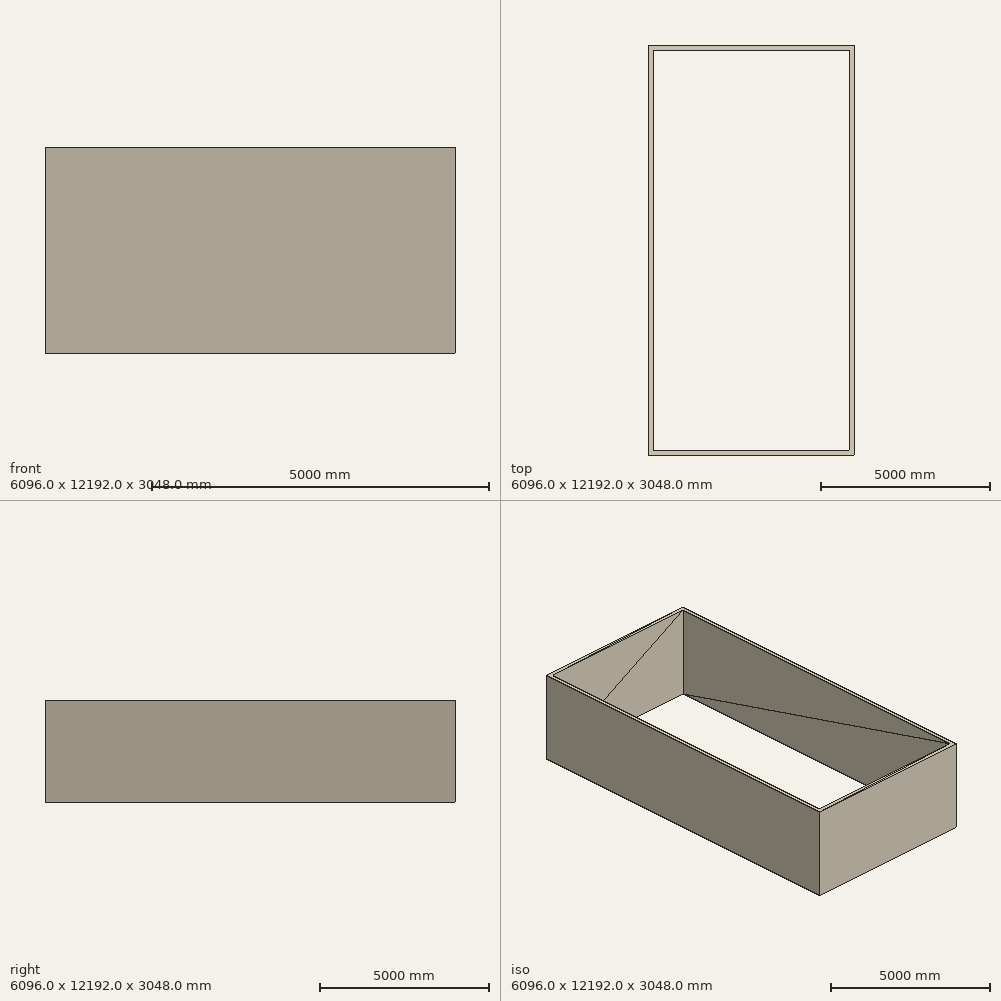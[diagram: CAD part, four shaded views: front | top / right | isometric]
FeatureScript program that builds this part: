
annotation { "Feature Type Name" : "Feature", "Feature Type Description" : "" }
export const myFeature = defineFeature(function(context is Context, id is Id, definition is map)
    precondition{}
    {
        {
            var Q0;
            Q0=qCreatedBy(makeId("Top.planeOp"),FACE);
            var sketch = newSketch(context, id + "F0", { "sketchPlane" : qUnion([Q0])});
            skLineSegment(sketch, "E0.bottom", {"start": v(-3052.12, 10269.46) * mm, "end": v(3043.88, 10269.46) * mm});
            skLineSegment(sketch, "E0.top", {"start": v(-3052.12, -1922.54) * mm, "end": v(3043.88, -1922.54) * mm});
            skLineSegment(sketch, "E0.left", {"start": v(-3052.12, 10269.46) * mm, "end": v(-3052.12, -1922.54) * mm});
            skLineSegment(sketch, "E0.right", {"start": v(3043.88, 10269.46) * mm, "end": v(3043.88, -1922.54) * mm});
            skLineSegment(sketch, "E1.0", {"start": v(-2912.42, 10129.76) * mm, "end": v(2904.18, 10129.76) * mm});
            skLineSegment(sketch, "E1.1", {"start": v(-2912.42, 10129.76) * mm, "end": v(-2912.42, -1782.84) * mm});
            skLineSegment(sketch, "E1.2", {"start": v(-2912.42, -1782.84) * mm, "end": v(2904.18, -1782.84) * mm});
            skLineSegment(sketch, "E1.3", {"start": v(2904.18, 10129.76) * mm, "end": v(2904.18, -1782.84) * mm});
            skSolve(sketch);
        }
        {
            var Q0;
            Q0=makeQuery(id+"F0.imprint","IMPRINT",FACE,{"disambiguationData":[TD([[makeQuery(id+"F0.imprint","IMPRINT",EDGE,{"derivedFrom":sQuery(id+"F0.wireOp",EDGE,"E0.bottom")}),-1.0]])]});
            extrude(context, id + "F1", {"entities" : qUnion([Q0]), "depth" : 3048 * mm, "offsetDistance" : 25.4 * mm});
        }
        {
            var Q0;
            Q0=makeQuery(id+"F1.opExtrude","SWEPT_BODY",BODY,{"disambiguationData":[OSD([sQuery(id+"F0.wireOp",EDGE,"E0.bottom"),sQuery(id+"F0.wireOp",EDGE,"E0.top"),sQuery(id+"F0.wireOp",EDGE,"E0.left"),sQuery(id+"F0.wireOp",EDGE,"E0.right"),sQuery(id+"F0.wireOp",EDGE,"E1.0"),sQuery(id+"F0.wireOp",EDGE,"E1.1"),sQuery(id+"F0.wireOp",EDGE,"E1.2"),sQuery(id+"F0.wireOp",EDGE,"E1.3")])]});
            transform(context, id + "F2", {"entities" : qUnion([Q0]), "transformType" : TransformType.TRANSLATION_3D, "dx" : 0 * mm, "dy" : 0 * mm, "dz" : 0 * mm, "makeCopy" : true});
        }
    });
